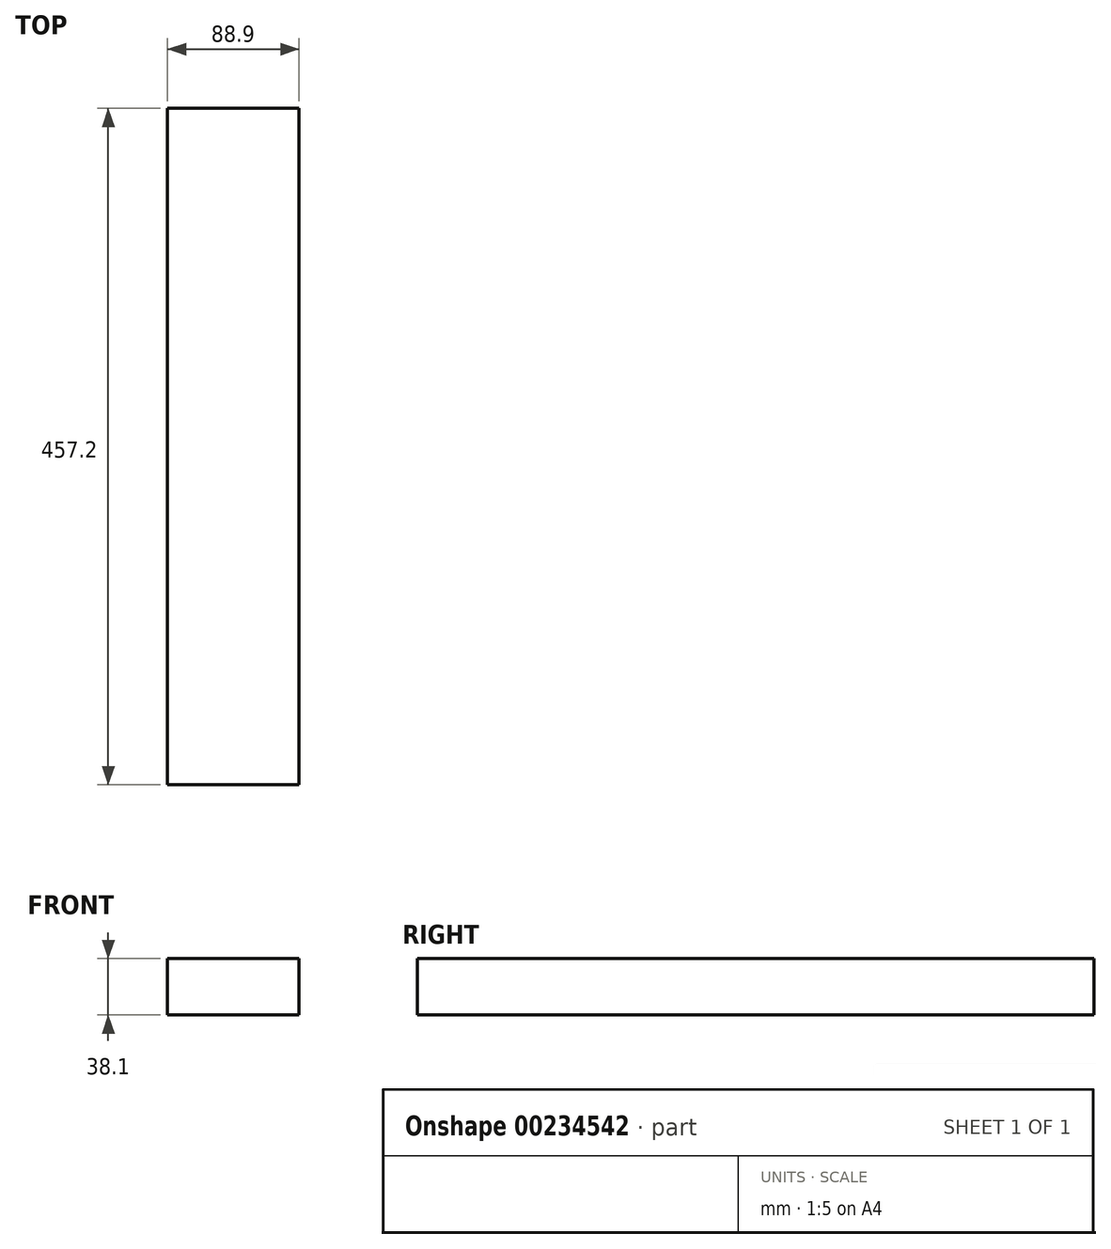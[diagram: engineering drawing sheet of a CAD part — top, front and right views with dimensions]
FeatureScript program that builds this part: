
annotation { "Feature Type Name" : "Feature", "Feature Type Description" : "" }
export const myFeature = defineFeature(function(context is Context, id is Id, definition is map)
    precondition{}
    {
        {
            var Q0;
            Q0=qCreatedBy(makeId("Top.planeOp"),FACE);
            var sketch = newSketch(context, id + "F0", { "sketchPlane" : qUnion([Q0])});
            skLineSegment(sketch, "E0.bottom", {"start": v(0, 0) * mm, "end": v(88.9, 0) * mm});
            skLineSegment(sketch, "E0.top", {"start": v(0, 457.2) * mm, "end": v(88.9, 457.2) * mm});
            skLineSegment(sketch, "E0.left", {"start": v(0, 0) * mm, "end": v(0, 457.2) * mm});
            skLineSegment(sketch, "E0.right", {"start": v(88.9, 0) * mm, "end": v(88.9, 457.2) * mm});
            skSolve(sketch);
        }
        {
            var Q0;
            Q0 = qSketchRegion(id + "F0", true);
            extrude(context, id + "F1", {"entities" : qUnion([Q0]), "depth" : 38.1 * mm});
        }
    });
